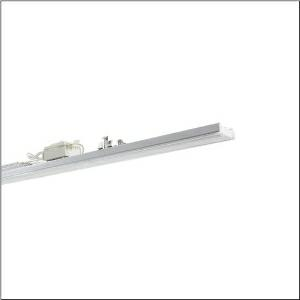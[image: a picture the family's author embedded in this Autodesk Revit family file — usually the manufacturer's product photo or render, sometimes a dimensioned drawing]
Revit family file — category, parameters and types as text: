
# Revit family: licross_11_recessed_ho_51tl18dn4d5m
name_source: partatom
category: Lighting Fixtures
units: mm (PartAtom-declared; Revit-internal decimal feet)

## family parameters
Cut with Voids When Loaded = No
Host = Face
Light Source = No
Part Type = Normal
Room Calculation Point = No
Round Connector Dimension = Use Diameter
Shared = No

## types (1)
- --- (1 x LED, 13890 lm, 76.8 W, 4000K)
    Apparent Load = 77 VA
    CIE Flux Codes = 78 94 99 100 100
    Color Rendering = 80
    Color Temperature = 4000K
    Default Elevation = 1800 mm
    Description = Licross 11 Recessed HO, luminaire insert, of sheet steel, coil coated, white, length: 1.500mm, width: 66mm, height: 67mm, LED rated luminous flux: 13.890lm, light colour: 840, SDCM (Standard Deviation of Colour Matching)MacAdam ≤ 2 SDCM (initial), control gear: DALI 2, with plug, 5-pole, with phase selection, mains connection: 220..240V, AC, 50/60Hz, rated input power: 77W, internal wiring halogen-free, primary light control with lens, of plastic, primary optical cover: cover, of PMMA, light emission: direct distribution, primary light characteristic: symmetric, protection rating (complete): IP40, insulation class (complete): insulation class I (protective earthing), certification: CE, ENEC, VDE, UKCA, protection symbol: D if used in an environment without relevant dust loads with corresponding accessories, impact resistance: IK06, permissible ambient temperature for indoor applications: -25..+30°C, corresponds to IFS (International Featured Standards) requirements for safety and quality in the food industry, reducing of maximum allowable ambient temperature of 5°C with ceiling mounting, LABS conformity tested according to VDMA 24364:2018-05, The light source and the operating device comply with the requirements of the Ecodesign Regulation (EU) 2019/2020 and are replaceable in accordance with this regulation, packaging unit: 1 piece
    Height = 58 mm
    Lamp = 1 x LED
    Lamp Light Flux = 13890 lm
    Lamp Power = 76.8 W
    Lamp count = 1
    Length = 1500 mm
    Luminous efficacy = 181 lm/W
    Manufacturer = Siteco
    ModVariant = No
    Model = 51TL18DN4D5M
    Mounting Place = Ceiling
    Mounting Type = Pendant
    Number of Poles = 1
    OnlyDefault = Yes
    Power Factor = 1
    Product Name = Licross 11 Recessed HO
    Product group = luminaire insert | ceiling pendant
    ProductGroupID = 901
    Protection Class = Protection class I
    Protection Degree = IP 40
    RLX_Detail_Level = 1
    RLX_Emergency_Light_Flux = 0 lm
    RLX_Emergency_Type = 0
    RLX_Emergency_Type_DB = No
    RlxData = <blob elided: 24909 chars, md5=7cacdddb>
    Socket = socket
    Standby Power = 0 W
    System Light Flux = 13890 lm
    System Power = 77 W
    Type Comments = factory setting: luminous flux: 100 % | dim-lin: 254 | 522 mA
    Type Image = l_1296930.jpg
    URL = http://relux.com
    VarID = @adj_030291
    Voltage = 0 V
    Weight = 0.00 kg
    Width = 66 mm

## geometry (parser evidence)
native form markers: Blend x4, Sweep x12
no freeform markers — native parametric forms only
